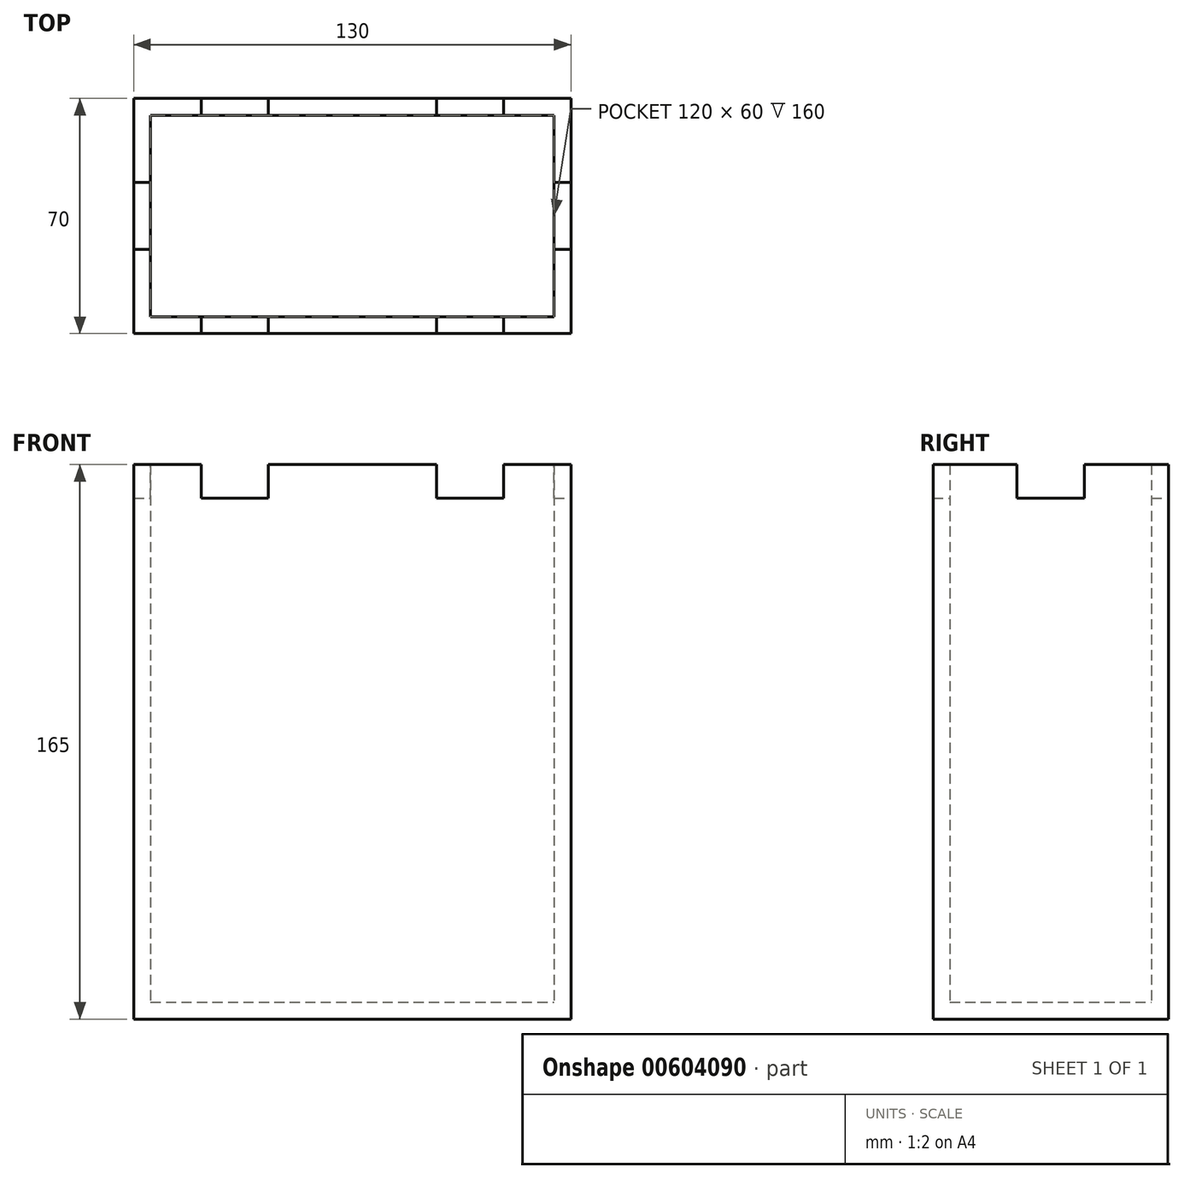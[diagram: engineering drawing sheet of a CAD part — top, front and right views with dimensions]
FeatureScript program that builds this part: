
annotation { "Feature Type Name" : "Feature", "Feature Type Description" : "" }
export const myFeature = defineFeature(function(context is Context, id is Id, definition is map)
    precondition{}
    {
        {
            var Q0;
            Q0=qCreatedBy(makeId("Top.planeOp"),FACE);
            var sketch = newSketch(context, id + "F0", { "sketchPlane" : qUnion([Q0])});
            skLineSegment(sketch, "E0.bottom", {"start": v(0, 0) * mm, "end": v(130, 0) * mm});
            skLineSegment(sketch, "E0.top", {"start": v(0, 70) * mm, "end": v(130, 70) * mm});
            skLineSegment(sketch, "E0.left", {"start": v(0, 0) * mm, "end": v(0, 70) * mm});
            skLineSegment(sketch, "E0.right", {"start": v(130, 0) * mm, "end": v(130, 70) * mm});
            skSolve(sketch);
        }
        {
            var Q0;
            Q0 = qSketchRegion(id + "F0", true);
            extrude(context, id + "F1", {"entities" : qUnion([Q0]), "depth" : 5 * mm, "offsetDistance" : 25.4 * mm});
        }
        {
            var Q0;
            Q0=makeQuery(id+"F1.opExtrude","CAP_FACE",FACE,{"disambiguationData":[OSD([sQuery(id+"F0.wireOp",EDGE,"E0.bottom"),sQuery(id+"F0.wireOp",EDGE,"E0.top"),sQuery(id+"F0.wireOp",EDGE,"E0.left"),sQuery(id+"F0.wireOp",EDGE,"E0.right")])],"isStart":false});
            var sketch = newSketch(context, id + "F2", { "sketchPlane" : qUnion([Q0])});
            skLineSegment(sketch, "E1.bottom", {"start": v(5, 5) * mm, "end": v(125, 5) * mm});
            skLineSegment(sketch, "E1.top", {"start": v(5, 65) * mm, "end": v(125, 65) * mm});
            skLineSegment(sketch, "E1.left", {"start": v(5, 5) * mm, "end": v(5, 65) * mm});
            skLineSegment(sketch, "E1.right", {"start": v(125, 5) * mm, "end": v(125, 65) * mm});
            skLineSegment(sketch, "E2.bottom", {"start": v(0, 0) * mm, "end": v(130, 0) * mm});
            skLineSegment(sketch, "E2.top", {"start": v(0, 70) * mm, "end": v(130, 70) * mm});
            skLineSegment(sketch, "E2.left", {"start": v(0, 0) * mm, "end": v(0, 70) * mm});
            skLineSegment(sketch, "E2.right", {"start": v(130, 0) * mm, "end": v(130, 70) * mm});
            skSolve(sketch);
        }
        {
            var Q0;
            Q0 = qSketchRegion(id + "F2", true);
            extrude(context, id + "F3", {"entities" : qUnion([Q0]), "operationType" : NewBodyOperationType.ADD, "depth" : 160 * mm, "offsetDistance" : 25.4 * mm});
        }
        {
            var Q0;
            Q0=makeQuery(id+"F3.opExtrude","CAP_FACE",FACE,{"disambiguationData":[OSD([sQuery(id+"F2.wireOp",EDGE,"E1.bottom"),sQuery(id+"F2.wireOp",EDGE,"E1.top"),sQuery(id+"F2.wireOp",EDGE,"E1.left"),sQuery(id+"F2.wireOp",EDGE,"E1.right"),sQuery(id+"F2.wireOp",EDGE,"E2.bottom"),sQuery(id+"F2.wireOp",EDGE,"E2.top"),sQuery(id+"F2.wireOp",EDGE,"E2.left"),sQuery(id+"F2.wireOp",EDGE,"E2.right")])],"isStart":false});
            var sketch = newSketch(context, id + "F4", { "sketchPlane" : qUnion([Q0])});
            skLineSegment(sketch, "E3.bottom", {"start": v(20, 0) * mm, "end": v(40, 0) * mm});
            skLineSegment(sketch, "E3.top", {"start": v(20, 70) * mm, "end": v(40, 70) * mm});
            skLineSegment(sketch, "E3.left", {"start": v(20, 0) * mm, "end": v(20, 70) * mm});
            skLineSegment(sketch, "E3.right", {"start": v(40, 0) * mm, "end": v(40, 70) * mm});
            skLineSegment(sketch, "E4.bottom", {"start": v(90, 0) * mm, "end": v(110, 0) * mm});
            skLineSegment(sketch, "E4.top", {"start": v(90, 70) * mm, "end": v(110, 70) * mm});
            skLineSegment(sketch, "E4.left", {"start": v(90, 0) * mm, "end": v(90, 70) * mm});
            skLineSegment(sketch, "E4.right", {"start": v(110, 0) * mm, "end": v(110, 70) * mm});
            skLineSegment(sketch, "E5.bottom", {"start": v(0, 25) * mm, "end": v(130, 25) * mm});
            skLineSegment(sketch, "E5.top", {"start": v(0, 45) * mm, "end": v(130, 45) * mm});
            skLineSegment(sketch, "E5.left", {"start": v(0, 25) * mm, "end": v(0, 45) * mm});
            skLineSegment(sketch, "E5.right", {"start": v(130, 25) * mm, "end": v(130, 45) * mm});
            skSolve(sketch);
        }
        {
            var Q0;
            Q0 = qSketchRegion(id + "F4", true);
            extrude(context, id + "F5", {"entities" : qUnion([Q0]), "operationType" : NewBodyOperationType.REMOVE, "oppositeDirection" : true, "depth" : 10 * mm, "offsetDistance" : 25.4 * mm});
        }
    });
